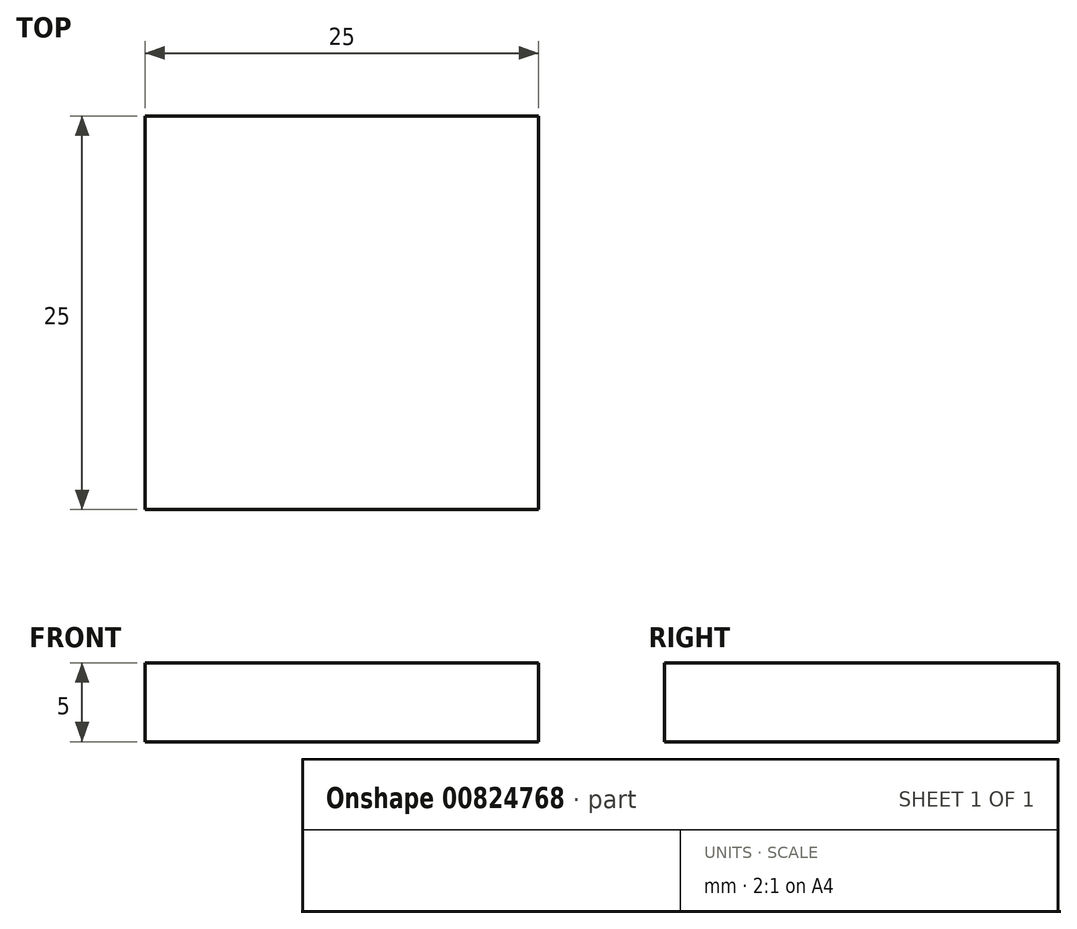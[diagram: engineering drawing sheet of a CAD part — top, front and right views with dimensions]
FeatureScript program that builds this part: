
annotation { "Feature Type Name" : "Feature", "Feature Type Description" : "" }
export const myFeature = defineFeature(function(context is Context, id is Id, definition is map)
    precondition{}
    {
        {
            var Q0;
            Q0=qCreatedBy(makeId("Top.planeOp"),FACE);
            var sketch = newSketch(context, id + "F0", { "sketchPlane" : qUnion([Q0])});
            skLineSegment(sketch, "E0.bottom", {"start": v(12.5, 12.5) * mm, "end": v(-12.5, 12.5) * mm});
            skLineSegment(sketch, "E0.top", {"start": v(12.5, -12.5) * mm, "end": v(-12.5, -12.5) * mm});
            skLineSegment(sketch, "E0.left", {"start": v(12.5, 12.5) * mm, "end": v(12.5, -12.5) * mm});
            skLineSegment(sketch, "E0.right", {"start": v(-12.5, 12.5) * mm, "end": v(-12.5, -12.5) * mm});
            skPoint(sketch, "E0.middle", {"position": v(0, 0) * mm});
            skSolve(sketch);
        }
        {
            var Q0;
            Q0=makeQuery(id+"F0.imprint","IMPRINT",FACE,{"disambiguationData":[TD([[makeQuery(id+"F0.imprint","IMPRINT",EDGE,{"derivedFrom":sQuery(id+"F0.wireOp",EDGE,"E0.bottom")}),1.0]])]});
            extrude(context, id + "F1", {"entities" : qUnion([Q0]), "depth" : 5 * mm, "offsetDistance" : 25 * mm});
        }
    });
